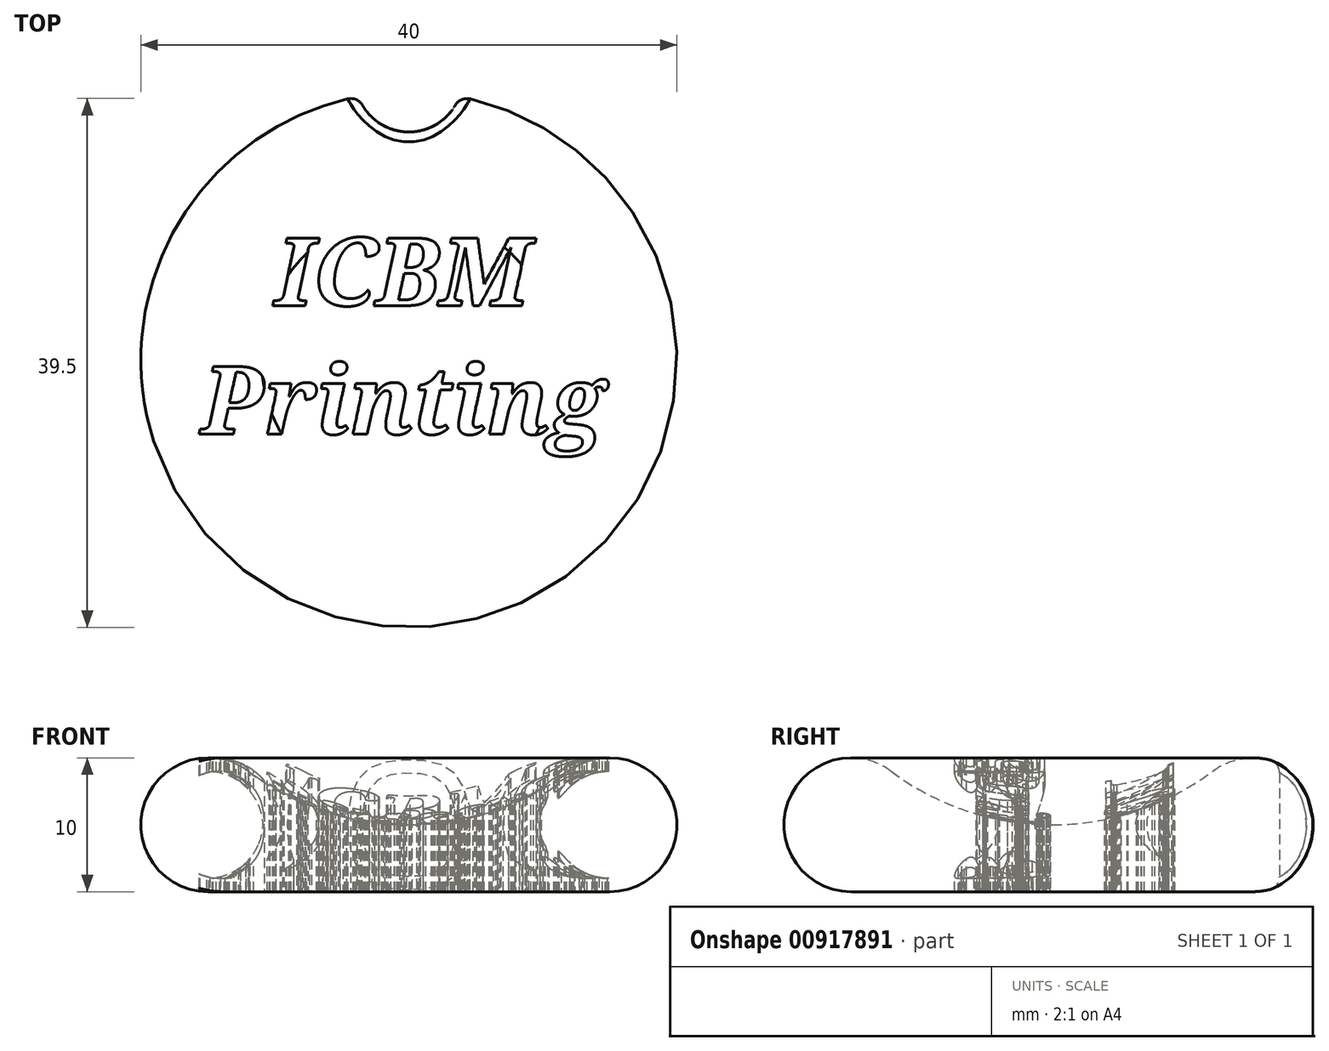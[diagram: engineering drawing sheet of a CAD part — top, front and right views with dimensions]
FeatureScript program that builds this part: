
annotation { "Feature Type Name" : "Feature", "Feature Type Description" : "" }
export const myFeature = defineFeature(function(context is Context, id is Id, definition is map)
    precondition{}
    {
        {
            var Q0;
            Q0=qCreatedBy(makeId("Front.planeOp"),FACE);
            var sketch = newSketch(context, id + "F0", { "sketchPlane" : qUnion([Q0])});
            skArc(sketch, "E0", {"start": v(-12, 9) * mm, "mid": v(-6.32, 6.03) * mm, "end": v(0, 5) * mm});
            skArc(sketch, "E1", {"start": v(-12, 9) * mm, "mid": v(-19.74, 6.58) * mm, "end": v(-15, 0) * mm});
            skLineSegment(sketch, "E2", {"start": v(-15, 0) * mm, "end": v(0, 0) * mm});
            skLineSegment(sketch, "E3", {"start": v(0, 0) * mm, "end": v(0, 5) * mm});
            skSolve(sketch);
        }
        {
            var Q0;
            Q0=makeQuery(id+"F0.imprint","IMPRINT",FACE,{"disambiguationData":[TD([[makeQuery(id+"F0.imprint","IMPRINT",EDGE,{"derivedFrom":sQuery(id+"F0.wireOp",EDGE,"E0")}),-1.0]])]});
            var Q1;
            Q1=sQuery(id+"F0.wireOp",EDGE,"E3");
            revolve(context, id + "F1", {"surfaceOperationType" : NewSurfaceOperationType.NEW, "entities" : qUnion([Q0]), "axis" : qUnion([Q1]), "revolveType" : RevolveType.FULL});
        }
        {
            var Q0;
            Q0=qCreatedBy(makeId("Top.planeOp"),FACE);
            cPlane(context, id + "F2", {"entities" : qUnion([Q0]), "cplaneType" : CPlaneType.OFFSET, "offset" : 11 * mm, "width" : 150 * mm, "height" : 150 * mm});
        }
        {
            var Q0;
            Q0=qCreatedBy(id+"F2.planeOp",FACE);
            var sketch = newSketch(context, id + "F3", { "sketchPlane" : qUnion([Q0])});
            skText(sketch, "E4", { "text": "   ICBM\nPrinting", "fontName": "NotoSerif-BoldItalic.ttf"});
            const initialGuessF3  = {"E4": [-0.0155, 0.00403, 1, 0, 0.00508]};
            skSetInitialGuess(sketch, initialGuessF3);
            skSolve(sketch);
        }
        {
            var Q0;
            Q0 = qSketchRegion(id + "F3", true);
            extrude(context, id + "F4", {"entities" : qUnion([Q0]), "operationType" : NewBodyOperationType.REMOVE, "oppositeDirection" : true, "depth" : 25 * mm, "offsetDistance" : 25 * mm});
        }
        {
            var Q0;
            Q0=qCreatedBy(makeId("Front.planeOp"),FACE);
            var sketch = newSketch(context, id + "F5", { "sketchPlane" : qUnion([Q0])});
            skCircle(sketch, "E5", {"center": v(-15, 5) * mm, "radius": 4 * mm});
            skSolve(sketch);
        }
        {
            var Q0;
            Q0 = qSketchRegion(id + "F5", true);
            var Q1;
            Q1=sQuery(id+"F0.wireOp",EDGE,"E3");
            revolve(context, id + "F6", {"operationType" : NewBodyOperationType.ADD, "surfaceOperationType" : NewSurfaceOperationType.NEW, "entities" : qUnion([Q0]), "axis" : qUnion([Q1]), "revolveType" : RevolveType.FULL});
        }
        {
            var Q0;
            Q0=qCreatedBy(makeId("Top.planeOp"),FACE);
            var sketch = newSketch(context, id + "F7", { "sketchPlane" : qUnion([Q0])});
            skCircle(sketch, "E6", {"center": v(0, 21) * mm, "radius": 4 * mm});
            skSolve(sketch);
        }
        {
            var Q0;
            Q0 = qSketchRegion(id + "F7", true);
            extrude(context, id + "F8", {"entities" : qUnion([Q0]), "operationType" : NewBodyOperationType.REMOVE, "depth" : 25 * mm, "offsetDistance" : 25 * mm});
        }
        {
            var Q0;
            Q0=makeQuery(id+"F8.boolean.opBoolean","INTERSECT",EDGE,{"derivedFrom":[makeQuery(id+"F4.boolean.opBoolean","SPLIT",FACE,{"disambiguationData":[TD([makeQuery(id+"F1.opRevolve","SWEPT_FACE",FACE,{"disambiguationData":[OSD([sQuery(id+"F0.wireOp",EDGE,"E0")])]}),makeQuery(id+"F1.opRevolve","SWEPT_FACE",FACE,{"disambiguationData":[OSD([sQuery(id+"F0.wireOp",EDGE,"E2")])]}),makeQuery(id+"F4.opExtrude","SWEPT_FACE",FACE,{"disambiguationData":[OSD([sQuery(id+"F3.wireOp",EDGE,"E4.sketch_text.stroke-6")])]}),makeQuery(id+"F4.opExtrude","SWEPT_FACE",FACE,{"disambiguationData":[OSD([sQuery(id+"F3.wireOp",EDGE,"E4.sketch_text.stroke-7")])]}),makeQuery(id+"F4.opExtrude","SWEPT_FACE",FACE,{"disambiguationData":[OSD([sQuery(id+"F3.wireOp",EDGE,"E4.sketch_text.stroke-8")])]}),makeQuery(id+"F4.opExtrude","SWEPT_FACE",FACE,{"disambiguationData":[OSD([sQuery(id+"F3.wireOp",EDGE,"E4.sketch_text.stroke-9")])]}),makeQuery(id+"F4.opExtrude","SWEPT_FACE",FACE,{"disambiguationData":[OSD([sQuery(id+"F3.wireOp",EDGE,"E4.sketch_text.stroke-10")])]}),makeQuery(id+"F4.opExtrude","SWEPT_FACE",FACE,{"disambiguationData":[OSD([sQuery(id+"F3.wireOp",EDGE,"E4.sketch_text.stroke-11")])]}),makeQuery(id+"F4.opExtrude","SWEPT_FACE",FACE,{"disambiguationData":[OSD([sQuery(id+"F3.wireOp",EDGE,"E4.sketch_text.stroke-12")])]}),makeQuery(id+"F4.opExtrude","SWEPT_FACE",FACE,{"disambiguationData":[OSD([sQuery(id+"F3.wireOp",EDGE,"E4.sketch_text.stroke-13")])]}),makeQuery(id+"F4.opExtrude","SWEPT_FACE",FACE,{"disambiguationData":[OSD([sQuery(id+"F3.wireOp",EDGE,"E4.sketch_text.stroke-14")])]}),makeQuery(id+"F4.opExtrude","SWEPT_FACE",FACE,{"disambiguationData":[OSD([sQuery(id+"F3.wireOp",EDGE,"E4.sketch_text.stroke-15")])]}),makeQuery(id+"F4.opExtrude","SWEPT_FACE",FACE,{"disambiguationData":[OSD([sQuery(id+"F3.wireOp",EDGE,"E4.sketch_text.stroke-120")])]}),makeQuery(id+"F4.opExtrude","SWEPT_FACE",FACE,{"disambiguationData":[OSD([sQuery(id+"F3.wireOp",EDGE,"E4.sketch_text.stroke-121")])]}),makeQuery(id+"F4.opExtrude","SWEPT_FACE",FACE,{"disambiguationData":[OSD([sQuery(id+"F3.wireOp",EDGE,"E4.sketch_text.stroke-122")])]}),makeQuery(id+"F4.opExtrude","SWEPT_FACE",FACE,{"disambiguationData":[OSD([sQuery(id+"F3.wireOp",EDGE,"E4.sketch_text.stroke-123")])]}),makeQuery(id+"F4.opExtrude","SWEPT_FACE",FACE,{"disambiguationData":[OSD([sQuery(id+"F3.wireOp",EDGE,"E4.sketch_text.stroke-124")])]}),makeQuery(id+"F4.opExtrude","SWEPT_FACE",FACE,{"disambiguationData":[OSD([sQuery(id+"F3.wireOp",EDGE,"E4.sketch_text.stroke-125")])]}),makeQuery(id+"F4.opExtrude","SWEPT_FACE",FACE,{"disambiguationData":[OSD([sQuery(id+"F3.wireOp",EDGE,"E4.sketch_text.stroke-126")])]}),makeQuery(id+"F4.opExtrude","SWEPT_FACE",FACE,{"disambiguationData":[OSD([sQuery(id+"F3.wireOp",EDGE,"E4.sketch_text.stroke-172")])]}),makeQuery(id+"F4.opExtrude","SWEPT_FACE",FACE,{"disambiguationData":[OSD([sQuery(id+"F3.wireOp",EDGE,"E4.sketch_text.stroke-173")])]}),makeQuery(id+"F4.opExtrude","SWEPT_FACE",FACE,{"disambiguationData":[OSD([sQuery(id+"F3.wireOp",EDGE,"E4.sketch_text.stroke-185")])]}),makeQuery(id+"F4.opExtrude","SWEPT_FACE",FACE,{"disambiguationData":[OSD([sQuery(id+"F3.wireOp",EDGE,"E4.sketch_text.stroke-186")])]}),makeQuery(id+"F4.opExtrude","SWEPT_FACE",FACE,{"disambiguationData":[OSD([sQuery(id+"F3.wireOp",EDGE,"E4.sketch_text.stroke-187")])]}),makeQuery(id+"F4.opExtrude","SWEPT_FACE",FACE,{"disambiguationData":[OSD([sQuery(id+"F3.wireOp",EDGE,"E4.sketch_text.stroke-188")])]}),makeQuery(id+"F4.opExtrude","SWEPT_FACE",FACE,{"disambiguationData":[OSD([sQuery(id+"F3.wireOp",EDGE,"E4.sketch_text.stroke-189")])]}),makeQuery(id+"F4.opExtrude","SWEPT_FACE",FACE,{"disambiguationData":[OSD([sQuery(id+"F3.wireOp",EDGE,"E4.sketch_text.stroke-190")])]}),makeQuery(id+"F4.opExtrude","SWEPT_FACE",FACE,{"disambiguationData":[OSD([sQuery(id+"F3.wireOp",EDGE,"E4.sketch_text.stroke-191")])]}),makeQuery(id+"F4.opExtrude","SWEPT_FACE",FACE,{"disambiguationData":[OSD([sQuery(id+"F3.wireOp",EDGE,"E4.sketch_text.stroke-192")])]}),makeQuery(id+"F4.opExtrude","SWEPT_FACE",FACE,{"disambiguationData":[OSD([sQuery(id+"F3.wireOp",EDGE,"E4.sketch_text.stroke-193")])]}),makeQuery(id+"F4.opExtrude","SWEPT_FACE",FACE,{"disambiguationData":[OSD([sQuery(id+"F3.wireOp",EDGE,"E4.sketch_text.stroke-194")])]}),makeQuery(id+"F4.opExtrude","SWEPT_FACE",FACE,{"disambiguationData":[OSD([sQuery(id+"F3.wireOp",EDGE,"E4.sketch_text.stroke-195")])]}),makeQuery(id+"F4.opExtrude","SWEPT_FACE",FACE,{"disambiguationData":[OSD([sQuery(id+"F3.wireOp",EDGE,"E4.sketch_text.stroke-196")])]}),makeQuery(id+"F4.opExtrude","SWEPT_FACE",FACE,{"disambiguationData":[OSD([sQuery(id+"F3.wireOp",EDGE,"E4.sketch_text.stroke-197")])]}),makeQuery(id+"F4.opExtrude","SWEPT_FACE",FACE,{"disambiguationData":[OSD([sQuery(id+"F3.wireOp",EDGE,"E4.sketch_text.stroke-198")])]}),makeQuery(id+"F4.opExtrude","SWEPT_FACE",FACE,{"disambiguationData":[OSD([sQuery(id+"F3.wireOp",EDGE,"E4.sketch_text.stroke-199")])]}),makeQuery(id+"F4.opExtrude","SWEPT_FACE",FACE,{"disambiguationData":[OSD([sQuery(id+"F3.wireOp",EDGE,"E4.sketch_text.stroke-200")])]}),makeQuery(id+"F4.opExtrude","SWEPT_FACE",FACE,{"disambiguationData":[OSD([sQuery(id+"F3.wireOp",EDGE,"E4.sketch_text.stroke-201")])]}),makeQuery(id+"F4.opExtrude","SWEPT_FACE",FACE,{"disambiguationData":[OSD([sQuery(id+"F3.wireOp",EDGE,"E4.sketch_text.stroke-202")])]}),makeQuery(id+"F4.opExtrude","SWEPT_FACE",FACE,{"disambiguationData":[OSD([sQuery(id+"F3.wireOp",EDGE,"E4.sketch_text.stroke-203")])]}),makeQuery(id+"F4.opExtrude","SWEPT_FACE",FACE,{"disambiguationData":[OSD([sQuery(id+"F3.wireOp",EDGE,"E4.sketch_text.stroke-204")])]}),makeQuery(id+"F4.opExtrude","SWEPT_FACE",FACE,{"disambiguationData":[OSD([sQuery(id+"F3.wireOp",EDGE,"E4.sketch_text.stroke-205")])]}),makeQuery(id+"F4.opExtrude","SWEPT_FACE",FACE,{"disambiguationData":[OSD([sQuery(id+"F3.wireOp",EDGE,"E4.sketch_text.stroke-206")])]}),makeQuery(id+"F4.opExtrude","SWEPT_FACE",FACE,{"disambiguationData":[OSD([sQuery(id+"F3.wireOp",EDGE,"E4.sketch_text.stroke-207")])]}),makeQuery(id+"F4.opExtrude","SWEPT_FACE",FACE,{"disambiguationData":[OSD([sQuery(id+"F3.wireOp",EDGE,"E4.sketch_text.stroke-208")])]}),makeQuery(id+"F4.opExtrude","SWEPT_FACE",FACE,{"disambiguationData":[OSD([sQuery(id+"F3.wireOp",EDGE,"E4.sketch_text.stroke-209")])]}),makeQuery(id+"F4.opExtrude","SWEPT_FACE",FACE,{"disambiguationData":[OSD([sQuery(id+"F3.wireOp",EDGE,"E4.sketch_text.stroke-210")])]}),makeQuery(id+"F4.opExtrude","SWEPT_FACE",FACE,{"disambiguationData":[OSD([sQuery(id+"F3.wireOp",EDGE,"E4.sketch_text.stroke-216")])]}),makeQuery(id+"F4.opExtrude","SWEPT_FACE",FACE,{"disambiguationData":[OSD([sQuery(id+"F3.wireOp",EDGE,"E4.sketch_text.stroke-217")])]}),makeQuery(id+"F4.opExtrude","SWEPT_FACE",FACE,{"disambiguationData":[OSD([sQuery(id+"F3.wireOp",EDGE,"E4.sketch_text.stroke-218")])]}),makeQuery(id+"F4.opExtrude","SWEPT_FACE",FACE,{"disambiguationData":[OSD([sQuery(id+"F3.wireOp",EDGE,"E4.sketch_text.stroke-219")])]}),makeQuery(id+"F4.opExtrude","SWEPT_FACE",FACE,{"disambiguationData":[OSD([sQuery(id+"F3.wireOp",EDGE,"E4.sketch_text.stroke-220")])]}),makeQuery(id+"F4.opExtrude","SWEPT_FACE",FACE,{"disambiguationData":[OSD([sQuery(id+"F3.wireOp",EDGE,"E4.sketch_text.stroke-247")])]}),makeQuery(id+"F4.opExtrude","SWEPT_FACE",FACE,{"disambiguationData":[OSD([sQuery(id+"F3.wireOp",EDGE,"E4.sketch_text.stroke-248")])]}),makeQuery(id+"F4.opExtrude","SWEPT_FACE",FACE,{"disambiguationData":[OSD([sQuery(id+"F3.wireOp",EDGE,"E4.sketch_text.stroke-488")])]}),makeQuery(id+"F4.opExtrude","SWEPT_FACE",FACE,{"disambiguationData":[OSD([sQuery(id+"F3.wireOp",EDGE,"E4.sketch_text.stroke-489")])]}),makeQuery(id+"F4.opExtrude","SWEPT_FACE",FACE,{"disambiguationData":[OSD([sQuery(id+"F3.wireOp",EDGE,"E4.sketch_text.stroke-490")])]}),makeQuery(id+"F4.opExtrude","SWEPT_FACE",FACE,{"disambiguationData":[OSD([sQuery(id+"F3.wireOp",EDGE,"E4.sketch_text.stroke-491")])]}),makeQuery(id+"F4.opExtrude","SWEPT_FACE",FACE,{"disambiguationData":[OSD([sQuery(id+"F3.wireOp",EDGE,"E4.sketch_text.stroke-492")])]}),makeQuery(id+"F4.opExtrude","SWEPT_FACE",FACE,{"disambiguationData":[OSD([sQuery(id+"F3.wireOp",EDGE,"E4.sketch_text.stroke-493")])]}),makeQuery(id+"F4.opExtrude","SWEPT_FACE",FACE,{"disambiguationData":[OSD([sQuery(id+"F3.wireOp",EDGE,"E4.sketch_text.stroke-494")])]}),makeQuery(id+"F4.opExtrude","SWEPT_FACE",FACE,{"disambiguationData":[OSD([sQuery(id+"F3.wireOp",EDGE,"E4.sketch_text.stroke-495")])]}),makeQuery(id+"F4.opExtrude","SWEPT_FACE",FACE,{"disambiguationData":[OSD([sQuery(id+"F3.wireOp",EDGE,"E4.sketch_text.stroke-496")])]}),makeQuery(id+"F4.opExtrude","SWEPT_FACE",FACE,{"disambiguationData":[OSD([sQuery(id+"F3.wireOp",EDGE,"E4.sketch_text.stroke-497")])]}),makeQuery(id+"F4.opExtrude","SWEPT_FACE",FACE,{"disambiguationData":[OSD([sQuery(id+"F3.wireOp",EDGE,"E4.sketch_text.stroke-498")])]}),makeQuery(id+"F4.opExtrude","SWEPT_FACE",FACE,{"disambiguationData":[OSD([sQuery(id+"F3.wireOp",EDGE,"E4.sketch_text.stroke-499")])]}),makeQuery(id+"F4.opExtrude","SWEPT_FACE",FACE,{"disambiguationData":[OSD([sQuery(id+"F3.wireOp",EDGE,"E4.sketch_text.stroke-500")])]}),makeQuery(id+"F4.opExtrude","SWEPT_FACE",FACE,{"disambiguationData":[OSD([sQuery(id+"F3.wireOp",EDGE,"E4.sketch_text.stroke-501")])]}),makeQuery(id+"F4.opExtrude","SWEPT_FACE",FACE,{"disambiguationData":[OSD([sQuery(id+"F3.wireOp",EDGE,"E4.sketch_text.stroke-502")])]}),makeQuery(id+"F4.opExtrude","SWEPT_FACE",FACE,{"disambiguationData":[OSD([sQuery(id+"F3.wireOp",EDGE,"E4.sketch_text.stroke-503")])]}),makeQuery(id+"F4.opExtrude","SWEPT_FACE",FACE,{"disambiguationData":[OSD([sQuery(id+"F3.wireOp",EDGE,"E4.sketch_text.stroke-504")])]}),makeQuery(id+"F4.opExtrude","SWEPT_FACE",FACE,{"disambiguationData":[OSD([sQuery(id+"F3.wireOp",EDGE,"E4.sketch_text.stroke-505")])]}),makeQuery(id+"F4.opExtrude","SWEPT_FACE",FACE,{"disambiguationData":[OSD([sQuery(id+"F3.wireOp",EDGE,"E4.sketch_text.stroke-506")])]}),makeQuery(id+"F4.opExtrude","SWEPT_FACE",FACE,{"disambiguationData":[OSD([sQuery(id+"F3.wireOp",EDGE,"E4.sketch_text.stroke-507")])]}),makeQuery(id+"F4.opExtrude","SWEPT_FACE",FACE,{"disambiguationData":[OSD([sQuery(id+"F3.wireOp",EDGE,"E4.sketch_text.stroke-508")])]}),makeQuery(id+"F4.opExtrude","SWEPT_FACE",FACE,{"disambiguationData":[OSD([sQuery(id+"F3.wireOp",EDGE,"E4.sketch_text.stroke-509")])]}),makeQuery(id+"F4.opExtrude","SWEPT_FACE",FACE,{"disambiguationData":[OSD([sQuery(id+"F3.wireOp",EDGE,"E4.sketch_text.stroke-510")])]}),makeQuery(id+"F4.opExtrude","SWEPT_FACE",FACE,{"disambiguationData":[OSD([sQuery(id+"F3.wireOp",EDGE,"E4.sketch_text.stroke-511")])]}),makeQuery(id+"F4.opExtrude","SWEPT_FACE",FACE,{"disambiguationData":[OSD([sQuery(id+"F3.wireOp",EDGE,"E4.sketch_text.stroke-512")])]}),makeQuery(id+"F4.opExtrude","SWEPT_FACE",FACE,{"disambiguationData":[OSD([sQuery(id+"F3.wireOp",EDGE,"E4.sketch_text.stroke-513")])]}),makeQuery(id+"F4.opExtrude","SWEPT_FACE",FACE,{"disambiguationData":[OSD([sQuery(id+"F3.wireOp",EDGE,"E4.sketch_text.stroke-514")])]}),makeQuery(id+"F4.opExtrude","SWEPT_FACE",FACE,{"disambiguationData":[OSD([sQuery(id+"F3.wireOp",EDGE,"E4.sketch_text.stroke-515")])]}),makeQuery(id+"F4.opExtrude","SWEPT_FACE",FACE,{"disambiguationData":[OSD([sQuery(id+"F3.wireOp",EDGE,"E4.sketch_text.stroke-516")])]}),makeQuery(id+"F4.opExtrude","SWEPT_FACE",FACE,{"disambiguationData":[OSD([sQuery(id+"F3.wireOp",EDGE,"E4.sketch_text.stroke-517")])]}),makeQuery(id+"F4.opExtrude","SWEPT_FACE",FACE,{"disambiguationData":[OSD([sQuery(id+"F3.wireOp",EDGE,"E4.sketch_text.stroke-518")])]}),makeQuery(id+"F4.opExtrude","SWEPT_FACE",FACE,{"disambiguationData":[OSD([sQuery(id+"F3.wireOp",EDGE,"E4.sketch_text.stroke-519")])]}),makeQuery(id+"F4.opExtrude","SWEPT_FACE",FACE,{"disambiguationData":[OSD([sQuery(id+"F3.wireOp",EDGE,"E4.sketch_text.stroke-520")])]}),makeQuery(id+"F4.opExtrude","SWEPT_FACE",FACE,{"disambiguationData":[OSD([sQuery(id+"F3.wireOp",EDGE,"E4.sketch_text.stroke-521")])]}),makeQuery(id+"F4.opExtrude","SWEPT_FACE",FACE,{"disambiguationData":[OSD([sQuery(id+"F3.wireOp",EDGE,"E4.sketch_text.stroke-522")])]}),makeQuery(id+"F4.opExtrude","SWEPT_FACE",FACE,{"disambiguationData":[OSD([sQuery(id+"F3.wireOp",EDGE,"E4.sketch_text.stroke-523")])]}),makeQuery(id+"F4.opExtrude","SWEPT_FACE",FACE,{"disambiguationData":[OSD([sQuery(id+"F3.wireOp",EDGE,"E4.sketch_text.stroke-524")])]}),makeQuery(id+"F4.opExtrude","SWEPT_FACE",FACE,{"disambiguationData":[OSD([sQuery(id+"F3.wireOp",EDGE,"E4.sketch_text.stroke-525")])]}),makeQuery(id+"F4.opExtrude","SWEPT_FACE",FACE,{"disambiguationData":[OSD([sQuery(id+"F3.wireOp",EDGE,"E4.sketch_text.stroke-526")])]}),makeQuery(id+"F4.opExtrude","SWEPT_FACE",FACE,{"disambiguationData":[OSD([sQuery(id+"F3.wireOp",EDGE,"E4.sketch_text.stroke-527")])]}),makeQuery(id+"F4.opExtrude","SWEPT_FACE",FACE,{"disambiguationData":[OSD([sQuery(id+"F3.wireOp",EDGE,"E4.sketch_text.stroke-528")])]}),makeQuery(id+"F4.opExtrude","SWEPT_FACE",FACE,{"disambiguationData":[OSD([sQuery(id+"F3.wireOp",EDGE,"E4.sketch_text.stroke-529")])]}),makeQuery(id+"F4.opExtrude","SWEPT_FACE",FACE,{"disambiguationData":[OSD([sQuery(id+"F3.wireOp",EDGE,"E4.sketch_text.stroke-530")])]}),makeQuery(id+"F4.opExtrude","SWEPT_FACE",FACE,{"disambiguationData":[OSD([sQuery(id+"F3.wireOp",EDGE,"E4.sketch_text.stroke-531")])]}),makeQuery(id+"F4.opExtrude","SWEPT_FACE",FACE,{"disambiguationData":[OSD([sQuery(id+"F3.wireOp",EDGE,"E4.sketch_text.stroke-532")])]}),makeQuery(id+"F4.opExtrude","SWEPT_FACE",FACE,{"disambiguationData":[OSD([sQuery(id+"F3.wireOp",EDGE,"E4.sketch_text.stroke-533")])]}),makeQuery(id+"F4.opExtrude","SWEPT_FACE",FACE,{"disambiguationData":[OSD([sQuery(id+"F3.wireOp",EDGE,"E4.sketch_text.stroke-534")])]}),makeQuery(id+"F4.opExtrude","SWEPT_FACE",FACE,{"disambiguationData":[OSD([sQuery(id+"F3.wireOp",EDGE,"E4.sketch_text.stroke-535")])]}),makeQuery(id+"F4.opExtrude","SWEPT_FACE",FACE,{"disambiguationData":[OSD([sQuery(id+"F3.wireOp",EDGE,"E4.sketch_text.stroke-536")])]}),makeQuery(id+"F4.opExtrude","SWEPT_FACE",FACE,{"disambiguationData":[OSD([sQuery(id+"F3.wireOp",EDGE,"E4.sketch_text.stroke-537")])]}),makeQuery(id+"F4.opExtrude","SWEPT_FACE",FACE,{"disambiguationData":[OSD([sQuery(id+"F3.wireOp",EDGE,"E4.sketch_text.stroke-538")])]}),makeQuery(id+"F4.opExtrude","SWEPT_FACE",FACE,{"disambiguationData":[OSD([sQuery(id+"F3.wireOp",EDGE,"E4.sketch_text.stroke-539")])]}),makeQuery(id+"F4.opExtrude","SWEPT_FACE",FACE,{"disambiguationData":[OSD([sQuery(id+"F3.wireOp",EDGE,"E4.sketch_text.stroke-540")])]}),makeQuery(id+"F4.opExtrude","SWEPT_FACE",FACE,{"disambiguationData":[OSD([sQuery(id+"F3.wireOp",EDGE,"E4.sketch_text.stroke-541")])]}),makeQuery(id+"F4.opExtrude","SWEPT_FACE",FACE,{"disambiguationData":[OSD([sQuery(id+"F3.wireOp",EDGE,"E4.sketch_text.stroke-542")])]}),makeQuery(id+"F4.opExtrude","SWEPT_FACE",FACE,{"disambiguationData":[OSD([sQuery(id+"F3.wireOp",EDGE,"E4.sketch_text.stroke-543")])]}),makeQuery(id+"F4.opExtrude","SWEPT_FACE",FACE,{"disambiguationData":[OSD([sQuery(id+"F3.wireOp",EDGE,"E4.sketch_text.stroke-544")])]}),makeQuery(id+"F4.opExtrude","SWEPT_FACE",FACE,{"disambiguationData":[OSD([sQuery(id+"F3.wireOp",EDGE,"E4.sketch_text.stroke-545")])]}),makeQuery(id+"F4.opExtrude","SWEPT_FACE",FACE,{"disambiguationData":[OSD([sQuery(id+"F3.wireOp",EDGE,"E4.sketch_text.stroke-546")])]}),makeQuery(id+"F4.opExtrude","SWEPT_FACE",FACE,{"disambiguationData":[OSD([sQuery(id+"F3.wireOp",EDGE,"E4.sketch_text.stroke-547")])]}),makeQuery(id+"F4.opExtrude","SWEPT_FACE",FACE,{"disambiguationData":[OSD([sQuery(id+"F3.wireOp",EDGE,"E4.sketch_text.stroke-548")])]}),makeQuery(id+"F4.opExtrude","SWEPT_FACE",FACE,{"disambiguationData":[OSD([sQuery(id+"F3.wireOp",EDGE,"E4.sketch_text.stroke-549")])]})])],"derivedFrom":makeQuery(id+"F1.opRevolve","SWEPT_FACE",FACE,{"disambiguationData":[OSD([sQuery(id+"F0.wireOp",EDGE,"E1")])]})}),makeQuery(id+"F8.opExtrude","SWEPT_FACE",FACE,{"disambiguationData":[OSD([sQuery(id+"F7.wireOp",EDGE,"E6")])]})]});
            fillet(context, id + "F9", {"entities" : qUnion([Q0]), "radius" : 1 * mm, "tangentPropagation" : true, "allowEdgeOverflow" : false});
        }
    });
